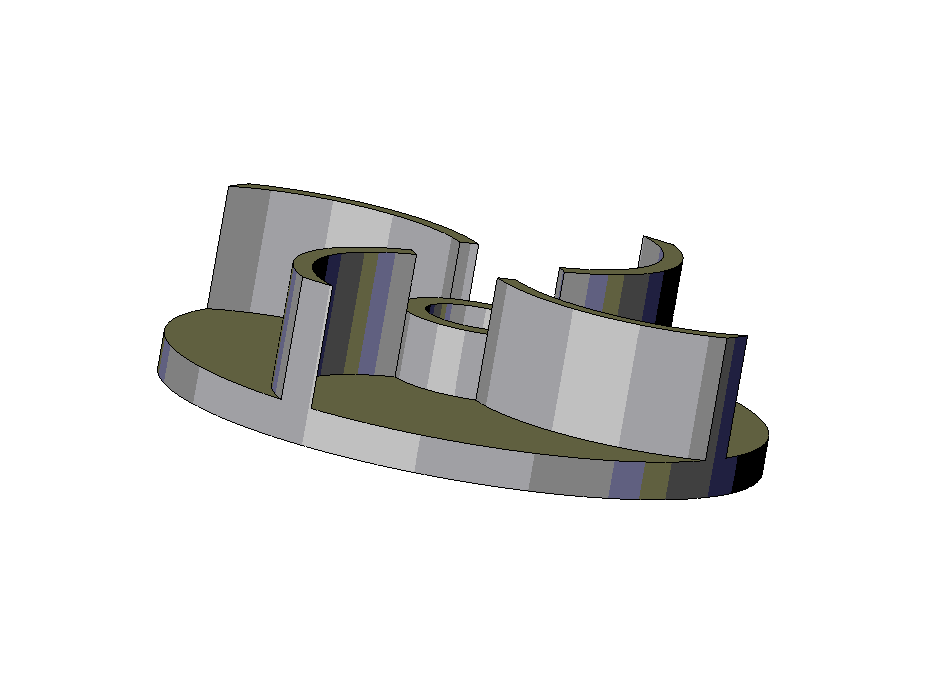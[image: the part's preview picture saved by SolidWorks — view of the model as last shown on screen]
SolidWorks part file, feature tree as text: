
SOLIDWORKS PART (.sldprt)
format: sldprt  version: not decoded by parser v0  size: 609,792 bytes
history: native  units: mm
features: sketch x5, extrude x3, cut_extrude x2, material x1, pattern_circular x1 (+12 scaffold rows collapsed)
feature tree (24):
  scaffold x12  (default folders/planes/origin — collapsed)
  material  "Material <not specified>"
  sketch  "Sketch1"  dims[D1=63.0mm]
  extrude  "Extrude1"  Depth=4mm
  sketch  "Sketch2"  dims[c1.D1=16.0mm c1.D2=70.0mm c1.D3=40.0mm c1.D4=18.0mm c2.D3=20.0mm c2.D2=70.0mm c2.D1=11.0mm c2.D4=12.0mm c2.D5=12.0mm c2.D6=8.0mm c3.D5=35.0mm c3.D2=1.0mm c3.D3=1.0mm]
  extrude  "Extrude3"  Depth=13mm
  sketch  "Sketch3"  dims[D1=16.0mm]
  pattern_circular  "CirPattern1"  Count=4 Angle=360deg
  cut_extrude  "Cut-Extrude1"  Depth=7mm
  sketch  "Sketch4"
  cut_extrude  "Cut-Extrude2"  [1 undecoded]
  sketch  "Sketch5"  dims[D1=16.0mm]
  extrude  "Extrude4"  Depth=7mm
decode coverage: 9 of 11 modeling features carry decoded parameters
note: 1 parameter value undecoded
note: suppression state not decoded; provenance and decode notes live in map.json
